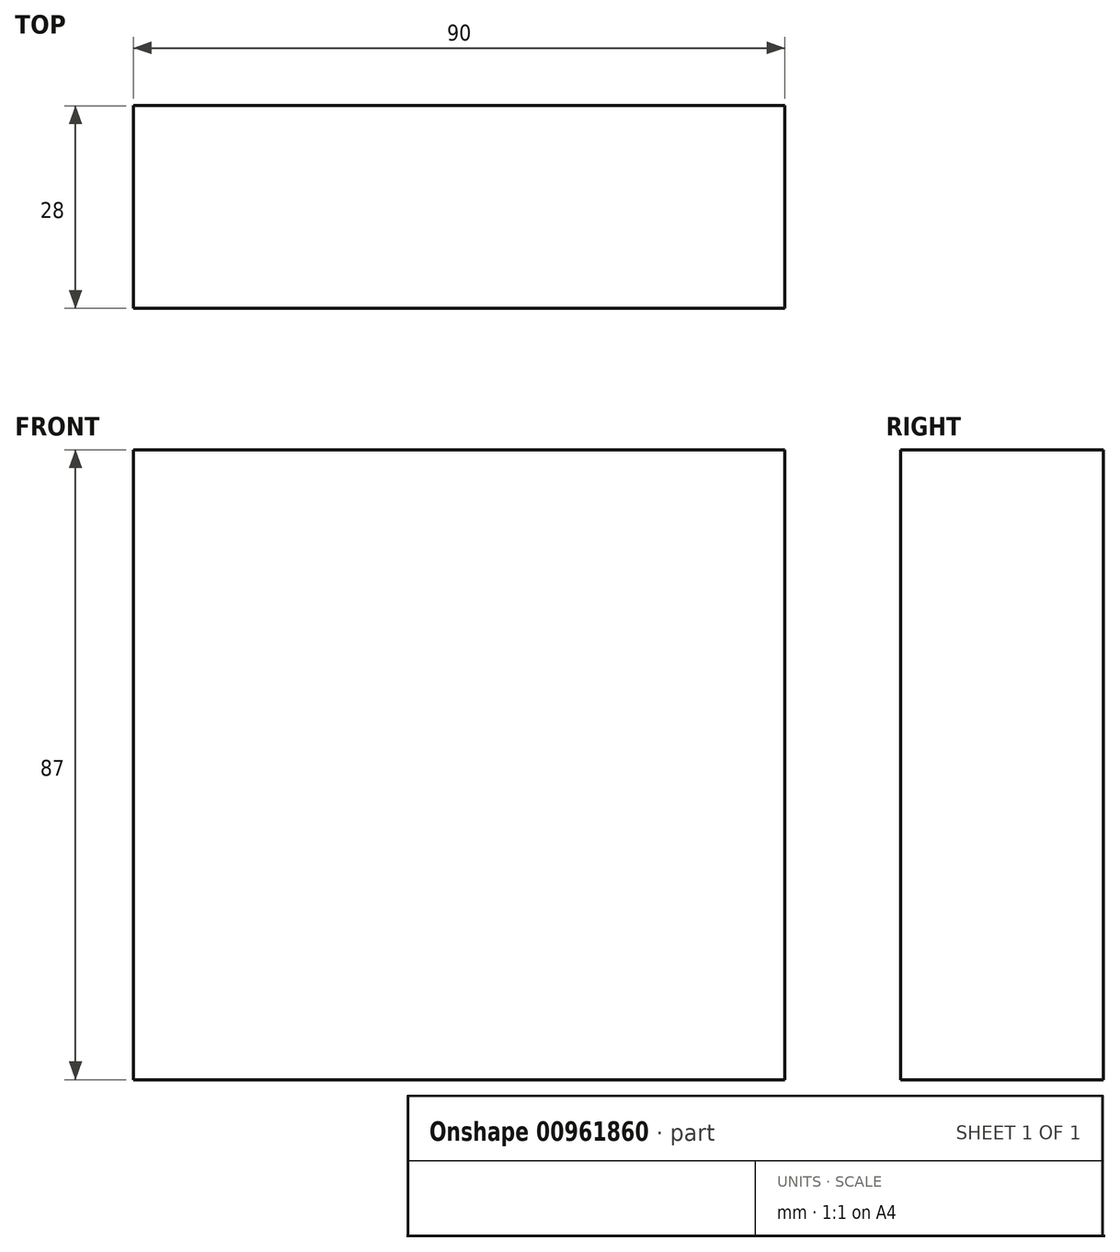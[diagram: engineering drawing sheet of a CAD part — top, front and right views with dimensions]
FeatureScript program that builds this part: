
annotation { "Feature Type Name" : "Feature", "Feature Type Description" : "" }
export const myFeature = defineFeature(function(context is Context, id is Id, definition is map)
    precondition{}
    {
        {
            var Q0;
            Q0=qCreatedBy(makeId("Top.planeOp"),FACE);
            var sketch = newSketch(context, id + "F0", { "sketchPlane" : qUnion([Q0])});
            skLineSegment(sketch, "E0.bottom", {"start": v(-33.53, 23.96) * mm, "end": v(56.47, 23.96) * mm});
            skLineSegment(sketch, "E0.top", {"start": v(-33.53, -4.04) * mm, "end": v(56.47, -4.04) * mm});
            skLineSegment(sketch, "E0.left", {"start": v(-33.53, 23.96) * mm, "end": v(-33.53, -4.04) * mm});
            skLineSegment(sketch, "E0.right", {"start": v(56.47, 23.96) * mm, "end": v(56.47, -4.04) * mm});
            skSolve(sketch);
        }
        {
            var Q0;
            Q0 = qSketchRegion(id + "F0", true);
            extrude(context, id + "F1", {"entities" : qUnion([Q0]), "depth" : 87 * mm, "offsetDistance" : 25 * mm});
        }
    });
